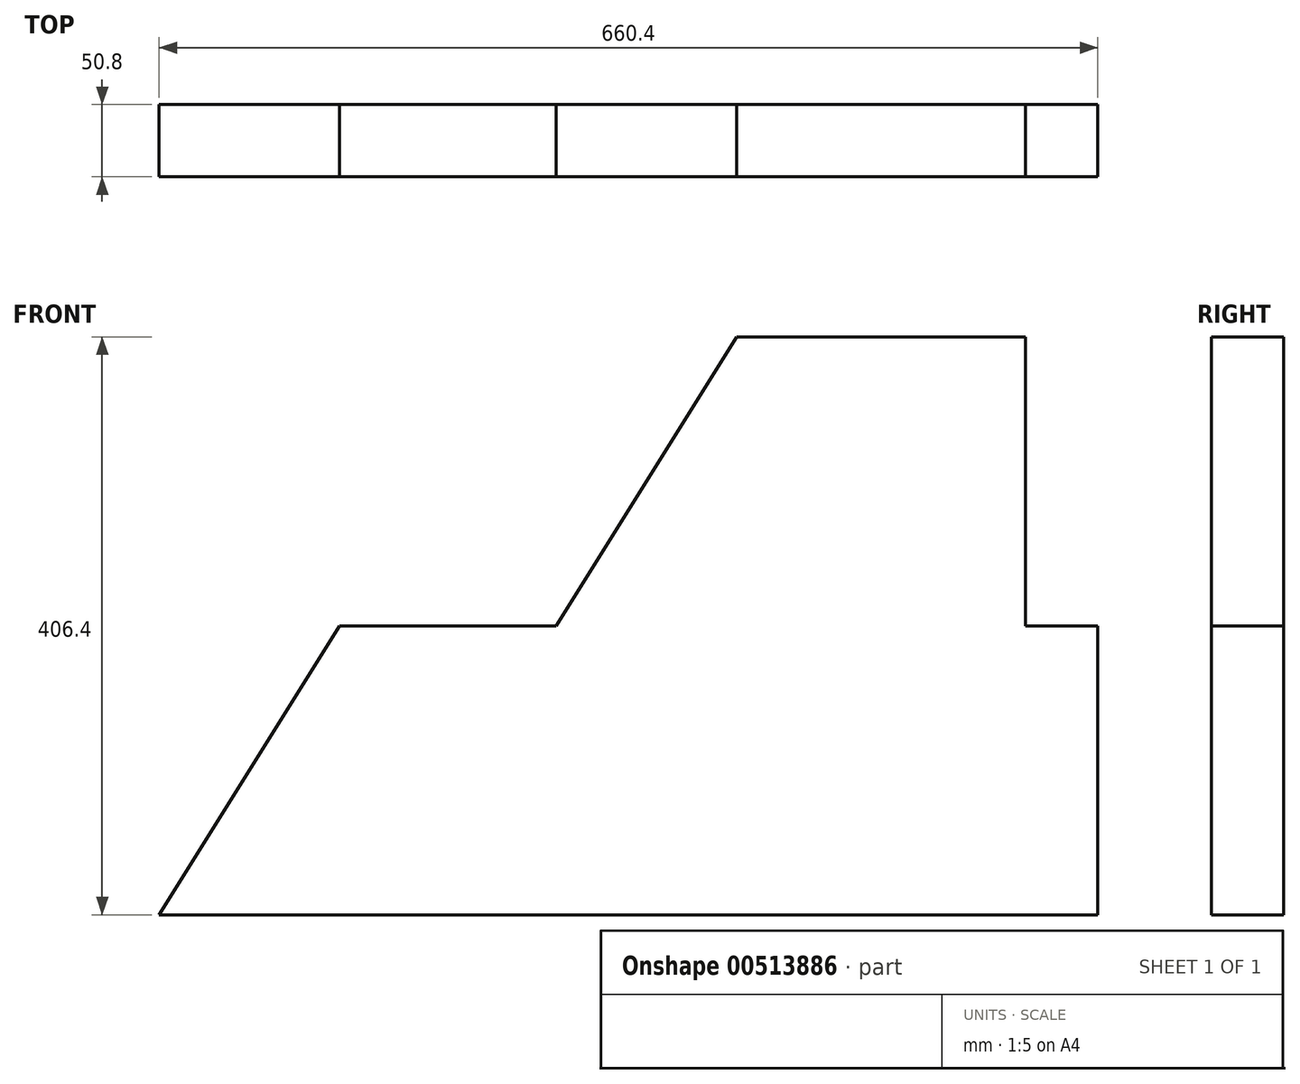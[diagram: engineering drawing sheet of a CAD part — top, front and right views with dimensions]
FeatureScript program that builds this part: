
annotation { "Feature Type Name" : "Feature", "Feature Type Description" : "" }
export const myFeature = defineFeature(function(context is Context, id is Id, definition is map)
    precondition{}
    {
        {
            var Q0;
            Q0=qCreatedBy(makeId("Front.planeOp"),FACE);
            var sketch = newSketch(context, id + "F0", { "sketchPlane" : qUnion([Q0])});
            skLineSegment(sketch, "E0", {"start": v(-76.37, 0) * mm, "end": v(584.03, 0) * mm});
            skLineSegment(sketch, "E1", {"start": v(584.03, 0) * mm, "end": v(584.03, 203.2) * mm});
            skLineSegment(sketch, "E2", {"start": v(584.03, 203.2) * mm, "end": v(533.23, 203.2) * mm});
            skLineSegment(sketch, "E3", {"start": v(533.23, 203.2) * mm, "end": v(533.23, 406.4) * mm});
            skLineSegment(sketch, "E4", {"start": v(533.23, 406.4) * mm, "end": v(330.03, 406.4) * mm});
            skLineSegment(sketch, "E5", {"start": v(330.03, 406.4) * mm, "end": v(203.03, 203.2) * mm});
            skLineSegment(sketch, "E6", {"start": v(203.03, 203.2) * mm, "end": v(50.63, 203.2) * mm});
            skLineSegment(sketch, "E7", {"start": v(50.63, 203.2) * mm, "end": v(-76.37, 0) * mm});
            skSolve(sketch);
        }
        {
            var Q0;
            Q0=makeQuery(id+"F0.imprint","IMPRINT",FACE,{"disambiguationData":[TD([[makeQuery(id+"F0.imprint","IMPRINT",EDGE,{"derivedFrom":sQuery(id+"F0.wireOp",EDGE,"E0")}),1.0]])]});
            extrude(context, id + "F1", {"entities" : qUnion([Q0]), "depth" : 50.8 * mm, "offsetDistance" : 25.4 * mm});
        }
    });
